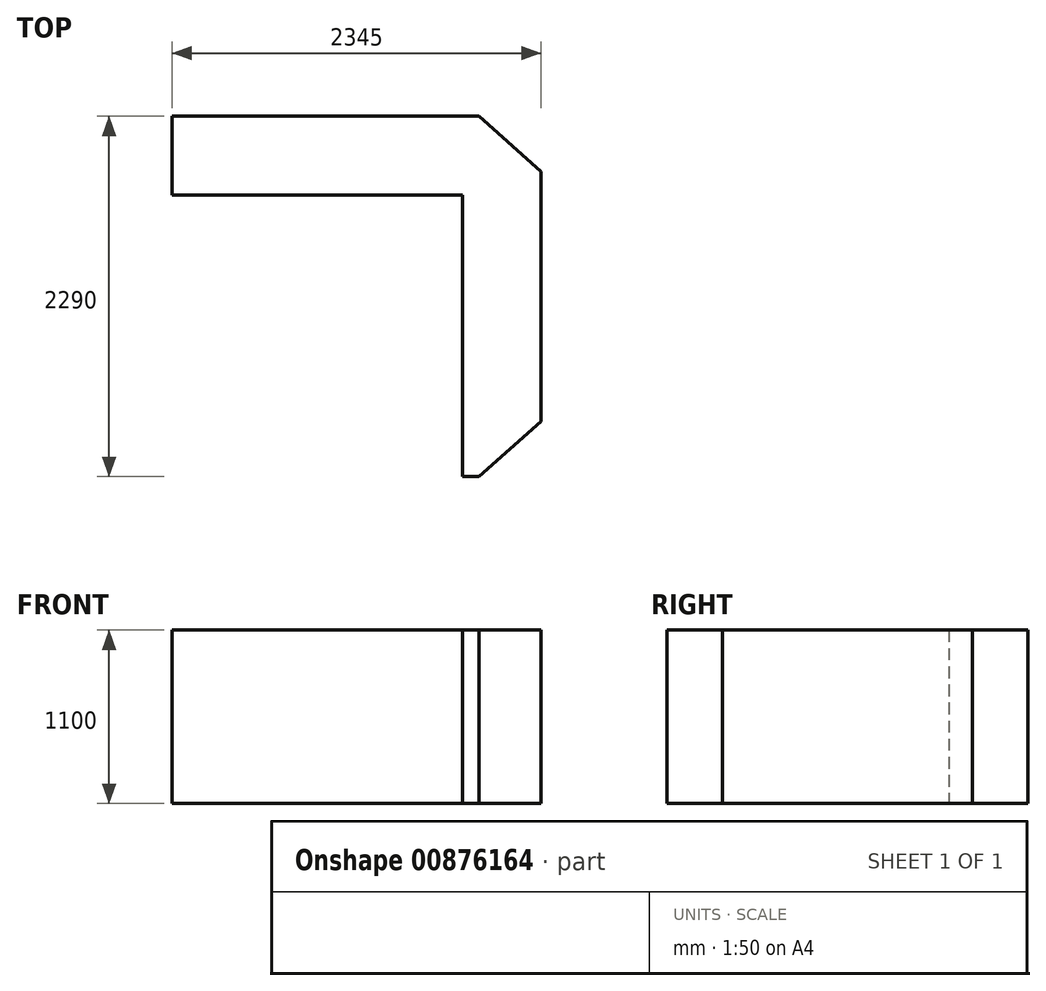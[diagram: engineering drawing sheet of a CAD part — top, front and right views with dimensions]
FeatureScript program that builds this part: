
annotation { "Feature Type Name" : "Feature", "Feature Type Description" : "" }
export const myFeature = defineFeature(function(context is Context, id is Id, definition is map)
    precondition{}
    {
        {
            var Q0;
            Q0=qCreatedBy(makeId("Top.planeOp"),FACE);
            var sketch = newSketch(context, id + "F0", { "sketchPlane" : qUnion([Q0])});
            skLineSegment(sketch, "E0.bottom", {"start": v(3150, -1200) * mm, "end": v(-3600, -1200) * mm});
            skLineSegment(sketch, "E0.top", {"start": v(3150, 1200) * mm, "end": v(627.5, 1200) * mm});
            skLineSegment(sketch, "E0.left", {"start": v(3600, -800) * mm, "end": v(3600, 800) * mm});
            skLineSegment(sketch, "E0.right", {"start": v(-3600, -1200) * mm, "end": v(-3600, 1200) * mm});
            skPoint(sketch, "E0.middle", {"position": v(0, 0) * mm});
            skLineSegment(sketch, "E1.0", {"start": v(3150, 1145) * mm, "end": v(627.5, 1145) * mm});
            skLineSegment(sketch, "E1.1", {"start": v(3545, -793.89) * mm, "end": v(3545, 793.89) * mm});
            skLineSegment(sketch, "E1.2", {"start": v(3150, -1145) * mm, "end": v(-3545, -1145) * mm});
            skLineSegment(sketch, "E1.3", {"start": v(-3545, -1145) * mm, "end": v(-3545, 1145) * mm});
            skLineSegment(sketch, "E2.bottom", {"start": v(-3545, 1145) * mm, "end": v(-2545, 1145) * mm});
            skLineSegment(sketch, "E2.top", {"start": v(-3545, -1145) * mm, "end": v(-2545, -1145) * mm});
            skLineSegment(sketch, "E2.left", {"start": v(-3545, 1145) * mm, "end": v(-3545, -1145) * mm});
            skLineSegment(sketch, "E2.right", {"start": v(-2545, 1145) * mm, "end": v(-2545, 245) * mm});
            skLineSegment(sketch, "E3.bottom", {"start": v(-2545, 1145) * mm, "end": v(-3545, 1145) * mm});
            skLineSegment(sketch, "E3.top", {"start": v(-2545, 245) * mm, "end": v(-3545, 245) * mm});
            skLineSegment(sketch, "E3.right", {"start": v(-3545, 1145) * mm, "end": v(-3545, 245) * mm});
            skLineSegment(sketch, "E4", {"start": v(-2545, -1145) * mm, "end": v(-2545, -505) * mm});
            skLineSegment(sketch, "E5", {"start": v(-2545, -505) * mm, "end": v(-2545, -1145) * mm});
            skLineSegment(sketch, "E6.0", {"start": v(-2515, 1145) * mm, "end": v(-2515, 245) * mm});
            skLineSegment(sketch, "E7.0", {"start": v(-2465, 1145) * mm, "end": v(-2465, 245) * mm});
            skLineSegment(sketch, "E8.0", {"start": v(-2435, 1145) * mm, "end": v(-2435, 245) * mm});
            skLineSegment(sketch, "E9", {"start": v(-2515, 245) * mm, "end": v(-2545, 245) * mm});
            skLineSegment(sketch, "E10", {"start": v(-2435, 245) * mm, "end": v(-2465, 245) * mm});
            skLineSegment(sketch, "E11.0", {"start": v(-2455, -1145) * mm, "end": v(-2455, -505) * mm});
            skLineSegment(sketch, "E12", {"start": v(-2545, -505) * mm, "end": v(-2455, -505) * mm});
            skLineSegment(sketch, "E13", {"start": v(3600, 800) * mm, "end": v(3600, 750) * mm});
            skLineSegment(sketch, "E14", {"start": v(3600, -800) * mm, "end": v(3600, -750) * mm});
            skLineSegment(sketch, "E15", {"start": v(3600, -750) * mm, "end": v(6297.68, 0) * mm});
            skLineSegment(sketch, "E16", {"start": v(6297.68, 0) * mm, "end": v(3600, 750) * mm});
            skLineSegment(sketch, "E17", {"start": v(-2435, 1145) * mm, "end": v(-1545, 1145) * mm});
            skLineSegment(sketch, "E18", {"start": v(-1545, 1145) * mm, "end": v(-1545, 545) * mm});
            skLineSegment(sketch, "E19", {"start": v(-1545, 545) * mm, "end": v(-2435, 545) * mm});
            skLineSegment(sketch, "E20.bottom", {"start": v(-1545, 545) * mm, "end": v(-1635, 545) * mm});
            skLineSegment(sketch, "E20.top", {"start": v(-1545, 635) * mm, "end": v(-1635, 635) * mm});
            skLineSegment(sketch, "E20.left", {"start": v(-1545, 545) * mm, "end": v(-1545, 635) * mm});
            skLineSegment(sketch, "E20.right", {"start": v(-1635, 545) * mm, "end": v(-1635, 635) * mm});
            skLineSegment(sketch, "E21.bottom", {"start": v(-3545, -1145) * mm, "end": v(-1545, -1145) * mm});
            skLineSegment(sketch, "E21.top", {"start": v(-3545, -505) * mm, "end": v(-1545, -505) * mm});
            skLineSegment(sketch, "E21.left", {"start": v(-3545, -1145) * mm, "end": v(-3545, -505) * mm});
            skLineSegment(sketch, "E21.right", {"start": v(-1545, -1145) * mm, "end": v(-1545, -505) * mm});
            skPoint(sketch, "E22.visualSharp", {"position": v(3545, 1145) * mm});
            skArc(sketch, "E22.filletArc", {"start": v(3545, 1140) * mm, "mid": v(3543.54, 1143.54) * mm, "end": v(3540, 1145) * mm});
            skLineSegment(sketch, "E23", {"start": v(3600, -800) * mm, "end": v(3150, -1200) * mm});
            skPoint(sketch, "E24.orphan", {"position": v(3600, -1200) * mm});
            skLineSegment(sketch, "E25", {"start": v(3150, -1145) * mm, "end": v(3545, -793.89) * mm});
            skLineSegment(sketch, "E26", {"start": v(3600, 800) * mm, "end": v(3150, 1200) * mm});
            skPoint(sketch, "E27.start.orphan", {"position": v(3600, 1200) * mm});
            skLineSegment(sketch, "E28", {"start": v(3150, 1145) * mm, "end": v(3545, 793.89) * mm});
            skLineSegment(sketch, "E29", {"start": v(3150, -1145) * mm, "end": v(1600, -1145) * mm});
            skLineSegment(sketch, "E30", {"start": v(1600, -1145) * mm, "end": v(1600, -545) * mm});
            skLineSegment(sketch, "E31", {"start": v(1600, -545) * mm, "end": v(3045, -545) * mm});
            skLineSegment(sketch, "E32", {"start": v(3045, -545) * mm, "end": v(3045, 645) * mm});
            skLineSegment(sketch, "E33", {"start": v(3045, 645) * mm, "end": v(1200, 645) * mm});
            skLineSegment(sketch, "E34", {"start": v(1200, 645) * mm, "end": v(1200, 1145) * mm});
            skLineSegment(sketch, "E35", {"start": v(-3600, 1200) * mm, "end": v(-972.5, 1200) * mm});
            skLineSegment(sketch, "E36.bottom", {"start": v(-1545, 1145) * mm, "end": v(-972.5, 1145) * mm});
            skLineSegment(sketch, "E36.top", {"start": v(-1545, 1200) * mm, "end": v(-972.5, 1200) * mm});
            skLineSegment(sketch, "E36.right", {"start": v(-972.5, 1145) * mm, "end": v(-972.5, 1200) * mm});
            skLineSegment(sketch, "E37.bottom", {"start": v(1200, 1145) * mm, "end": v(627.5, 1145) * mm});
            skLineSegment(sketch, "E37.top", {"start": v(1200, 1200) * mm, "end": v(627.5, 1200) * mm});
            skLineSegment(sketch, "E38.trimOffspring", {"start": v(-972.5, 1145) * mm, "end": v(-3545, 1145) * mm});
            skPoint(sketch, "E39.orphan", {"position": v(0, 1200) * mm});
            skLineSegment(sketch, "E40.trimOffspring", {"start": v(-972.5, 1200) * mm, "end": v(-3600, 1200) * mm});
            skLineSegment(sketch, "E41", {"start": v(627.5, 1200) * mm, "end": v(627.5, 1145) * mm});
            skLineSegment(sketch, "E42", {"start": v(3045, -545) * mm, "end": v(3045, -1145) * mm});
            skLineSegment(sketch, "E43.bottom", {"start": v(1600, -545) * mm, "end": v(1510, -545) * mm});
            skLineSegment(sketch, "E43.top", {"start": v(1600, -635) * mm, "end": v(1510, -635) * mm});
            skLineSegment(sketch, "E43.left", {"start": v(1600, -545) * mm, "end": v(1600, -635) * mm});
            skLineSegment(sketch, "E43.right", {"start": v(1510, -545) * mm, "end": v(1510, -635) * mm});
            skLineSegment(sketch, "E44.bottom", {"start": v(1600, -1145) * mm, "end": v(1100, -1145) * mm});
            skLineSegment(sketch, "E44.top", {"start": v(1600, -545) * mm, "end": v(1100, -545) * mm});
            skLineSegment(sketch, "E44.right", {"start": v(1100, -1145) * mm, "end": v(1100, -545) * mm});
            skLineSegment(sketch, "E45.bottom", {"start": v(-1545, -505) * mm, "end": v(-1145, -505) * mm});
            skLineSegment(sketch, "E45.top", {"start": v(-1545, -1145) * mm, "end": v(-1145, -1145) * mm});
            skLineSegment(sketch, "E45.left", {"start": v(-1545, -505) * mm, "end": v(-1545, -1145) * mm});
            skLineSegment(sketch, "E45.right", {"start": v(-1145, -505) * mm, "end": v(-1145, -1145) * mm});
            skText(sketch, "E46", { "text": "shower\n", "fontName": "OpenSans-Regular.ttf"});
            const initialGuessF0  = {"E46": [-3.49717, 0.84324, 1, 0, 0.17821]};
            skSetInitialGuess(sketch, initialGuessF0);
            skSolve(sketch);
        }
        {
            var Q0;
            Q0=makeQuery(id+"F0.imprint","IMPRINT",FACE,{"disambiguationData":[TD([[makeQuery(id+"F0.imprint","IMPRINT",EDGE,{"derivedFrom":sQuery(id+"F0.wireOp",EDGE,"E1.0")}),1.0]])]});
            extrude(context, id + "F1", {"entities" : qUnion([Q0]), "depth" : 1100 * mm, "offsetDistance" : 25 * mm});
        }
    });
